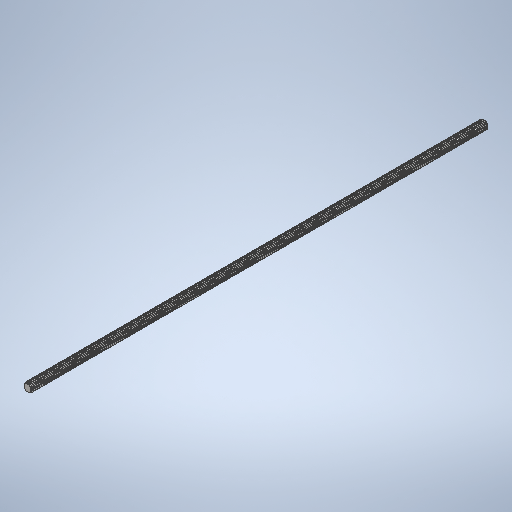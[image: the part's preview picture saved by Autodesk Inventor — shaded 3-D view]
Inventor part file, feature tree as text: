
AUTODESK INVENTOR PART (.ipt)
format: ipt  version: 2025.2 (Build 292293000, 293)  size: 1,661,952 bytes
history: native  units: mm
features: extrude x1, chamfer x1, other x1, pattern_circular x1
ambient origin geometry x8: Origin, YZ Plane, XZ Plane, XY Plane, X Axis, Y Axis, Z Axis, Center Point
bodies: Solid1 (feature_tree)
feature tree (4):
  extrude  "1000mm Rod"  Depth=420.0mm TaperAngle=0.0deg
  chamfer  "Chamfer1"  Distance=0.907143mm Angle=45.0deg
  other  "ACME Thread 2mm Pitch"
  pattern_circular  "4 Start"  [2 undecoded]
note: 2 required parameter values undecoded (feature->parameter linkage not recoverable at this tier; creation-order binding heuristic only, values carry confidence <= 0.55)
